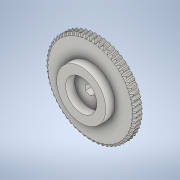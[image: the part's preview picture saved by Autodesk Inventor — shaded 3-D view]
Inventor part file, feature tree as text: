
AUTODESK INVENTOR PART (.ipt)
format: ipt  version: 2022.2 (Build 262287010, 287A)  size: 1,166,336 bytes
history: native  units: mm (DEFAULTED — no unit token found)
features: other x8, plane x3, sketch x3, extrude x2, pattern_circular x1
ambient origin geometry x5: Origin, X Axis, Y Axis, Z Axis, Center Point
bodies: Solid1 (feature_tree)
feature tree (17):
  other  "Tooth Plane"
  other  "Base Body Sketch"
  other  "Base Body"
  other  "Base Body2"
  plane  "Work Plane13"
  other  "Tooth"
  pattern_circular  "Tooth Pattern"  [2 undecoded]
  plane  "Work Plane14"
  plane  "Work Plane15"
  extrude  "Extrusion1"  Depth=12.954mm
  extrude  "Extrusion2"  Depth=12.954mm
  other  "Tooth Sketch"
  sketch  "Sketch8"  dims[d35=90.0deg]
  other  "Srf1"
  sketch  "Sketch9"  dims[d37=-0.996687mm]
  sketch  "Sketch10"  dims[d38=70.744372mm d39=3.490659mm d40=7.680818mm d41=10.106339mm d42=1.905mm d43=90.0deg d44=600.0mm d46=360.0deg d50=5.318254mm d68=70.744372mm d69=0.0mm d73=0.0mm d75=0.523599mm d77=121.276067mm d78=12.3mm d79=0.0mm d80=0.0mm d81=0.0mm d82=0.0mm d83=0.523599mm d84=0.0mm d85=180.0deg d86=70.744372mm d87=127.33987mm d89=16.170142mm d90=90.0deg d92=12.3mm d93=70.744372mm d94=44.45mm d95=12.7mm d96=12.7mm d97=0.0mm d98=12.954mm d99=0.0mm d100=0.0mm]
  other  "Pitch Diameter"
note: 2 required parameter values undecoded (feature->parameter linkage not recoverable at this tier; creation-order binding heuristic only, values carry confidence <= 0.55)
